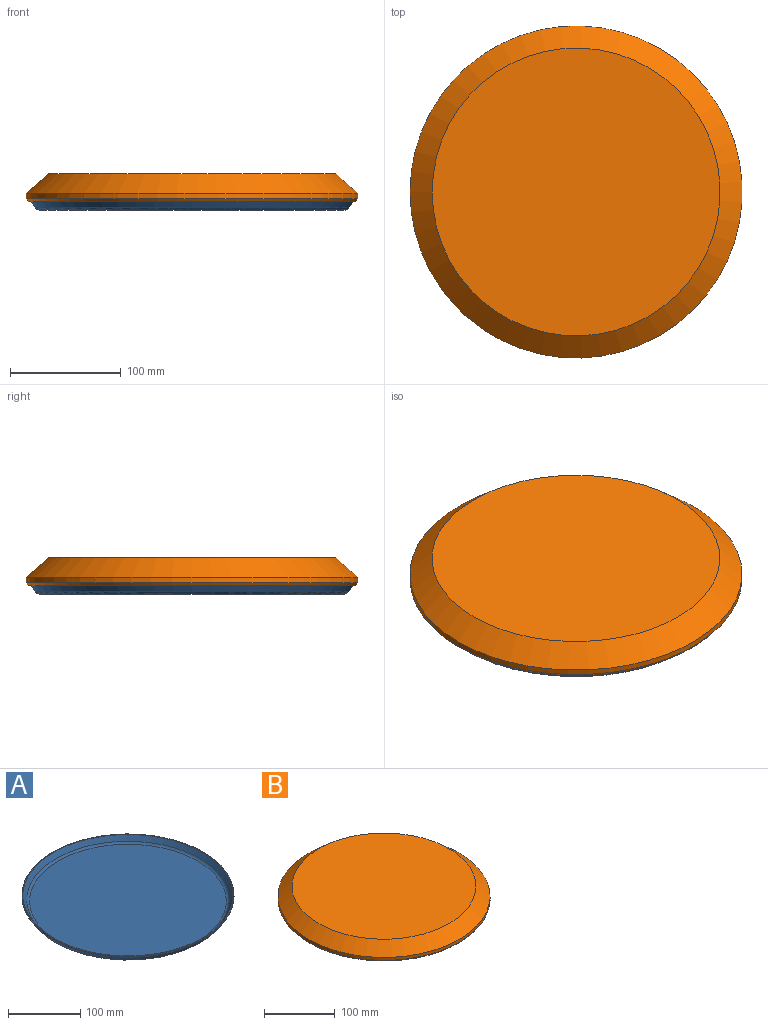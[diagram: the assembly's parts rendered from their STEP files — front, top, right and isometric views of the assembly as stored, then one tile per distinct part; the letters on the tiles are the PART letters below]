
ASSEMBLY  parts=2 mates=1
PART A: 9 faces, bbox 308.3x308.3x12 mm
  f0: cone r=145.81mm half-angle=35deg, axis (0,0,1), area 8407.6mm2, adj f1,f8
  f1: cylinder r=145.81mm len=291.63mm, axis (0,0,-1), area 191mm2, adj f0,f2
  f2: plane 294x294mm, normal (0,0,1), area 1092.1mm2, adj f1,f3
  f3: cylinder r=147mm len=294mm, axis (0,0,-1), area 1847.3mm2, adj f2,f4
  f4: cone r=147mm half-angle=35deg, axis (0,0,1), area 8703.7mm2, adj f3,f7
  f5: plane 274.79x274.79mm, normal (0,0,-1), area 59306.5mm2, adj f7
  f6: plane 272.71x272.71mm, normal (0,0,1), area 58411mm2, adj f8
  f7: torus R=137.4mm, axis (0,0,-1), area 4211.1mm2, adj f4,f5
  f8: torus R=136.36mm, axis (0,0,-1), area 4179.7mm2, adj f0,f6
PART B: 7 faces, bbox 300x300x25 mm
  f0: cone r=130mm half-angle=48.8deg, axis (0,0,-1), area 23376.9mm2, adj f1,f6
  f1: cylinder r=150mm len=300mm, axis (0,0,-1), area 4712.4mm2, adj f0,f2
  f2: cone r=150mm half-angle=38.7deg, axis (0,0,1), area 2997.3mm2, adj f1,f3
  f3: cylinder r=148mm len=296mm, axis (0,0,-1), area 6130.4mm2, adj f2,f4
  f4: cone r=129.25mm half-angle=48.8deg, axis (0,0,-1), area 21702.2mm2, adj f3,f5
  f5: plane 258.5x258.5mm, normal (0,0,-1), area 52480.9mm2, adj f4
  f6: plane 260x260mm, normal (0,0,1), area 53092.9mm2, adj f0
PLACE A t=(-341.58,-81.57,-86.33)mm
PLACE B t=(-341.58,-81.57,-88.62)mm
MATE revolute A.f0 <-> B.f0  axis (0,0,-1) through (-324.54,-81.57,-72.49)mm
